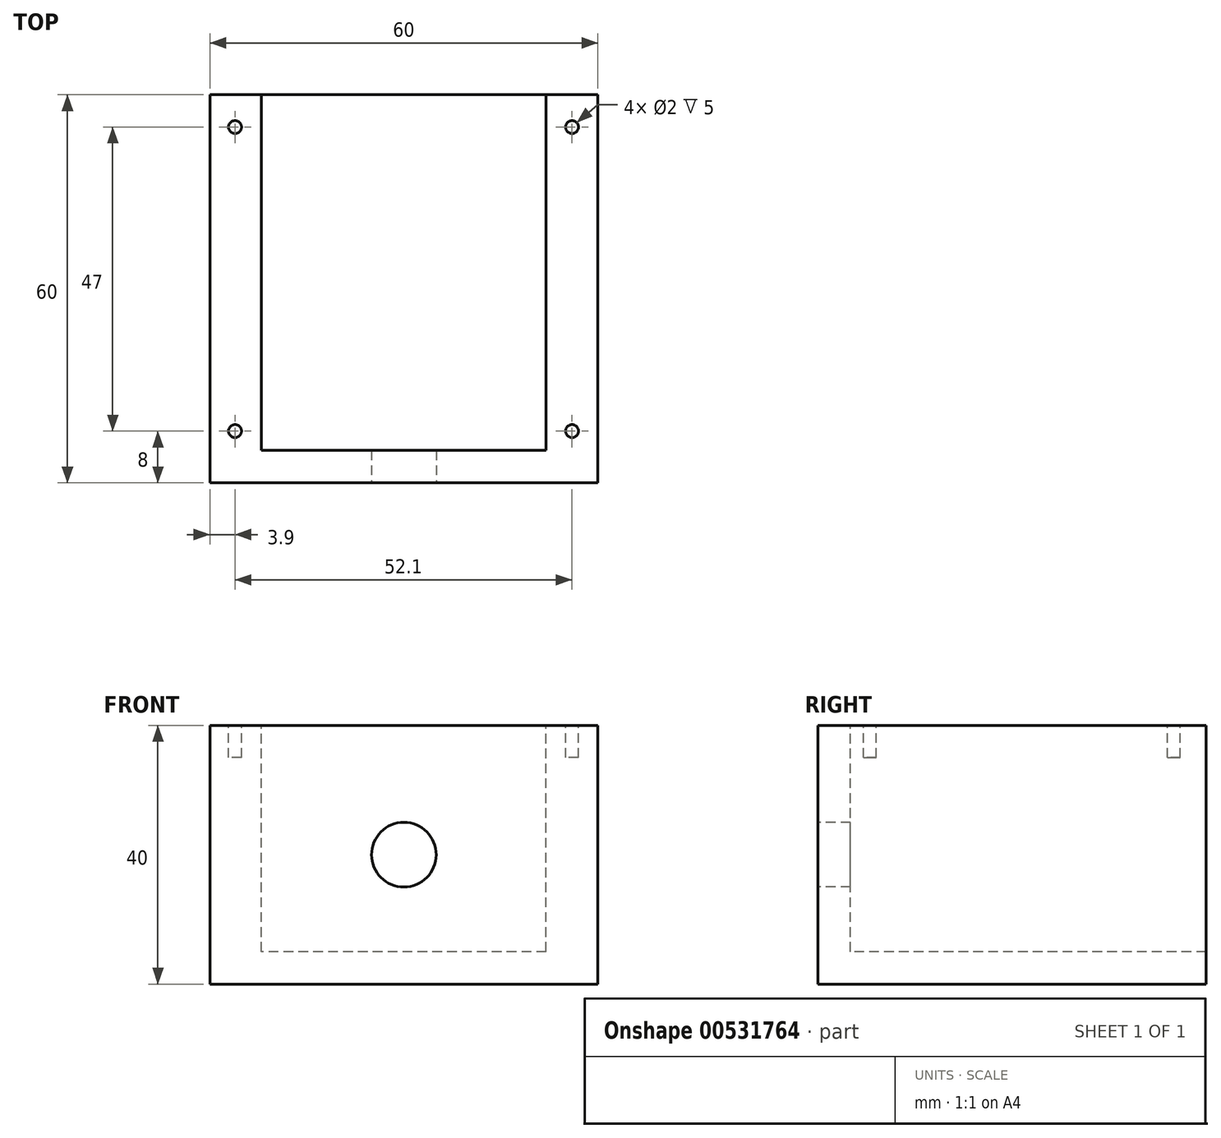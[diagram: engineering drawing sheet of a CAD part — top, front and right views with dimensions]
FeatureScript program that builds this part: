
annotation { "Feature Type Name" : "Feature", "Feature Type Description" : "" }
export const myFeature = defineFeature(function(context is Context, id is Id, definition is map)
    precondition{}
    {
        {
            var Q0;
            Q0=qCreatedBy(makeId("Front.planeOp"),FACE);
            var sketch = newSketch(context, id + "F0", { "sketchPlane" : qUnion([Q0])});
            skLineSegment(sketch, "E0.bottom", {"start": v(30, 20) * mm, "end": v(-30, 20) * mm});
            skLineSegment(sketch, "E0.top", {"start": v(30, -20) * mm, "end": v(-30, -20) * mm});
            skLineSegment(sketch, "E0.left", {"start": v(30, 20) * mm, "end": v(30, -20) * mm});
            skLineSegment(sketch, "E0.right", {"start": v(-30, 20) * mm, "end": v(-30, -20) * mm});
            skPoint(sketch, "E0.middle", {"position": v(0, 0) * mm});
            skSolve(sketch);
        }
        {
            var Q0;
            Q0 = qSketchRegion(id + "F0", true);
            extrude(context, id + "F1", {"entities" : qUnion([Q0]), "depth" : 60 * mm, "offsetDistance" : 25 * mm});
        }
        {
            var Q0;
            Q0=makeQuery(id+"F1.opExtrude","SWEPT_FACE",FACE,{"disambiguationData":[OSD([sQuery(id+"F0.wireOp",EDGE,"E0.bottom")])]});
            var sketch = newSketch(context, id + "F2", { "sketchPlane" : qUnion([Q0])});
            skLineSegment(sketch, "E1.bottom", {"start": v(-22, 0) * mm, "end": v(22, 0) * mm});
            skLineSegment(sketch, "E1.top", {"start": v(-22, -55) * mm, "end": v(22, -55) * mm});
            skLineSegment(sketch, "E1.left", {"start": v(-22, 0) * mm, "end": v(-22, -55) * mm});
            skLineSegment(sketch, "E1.right", {"start": v(22, 0) * mm, "end": v(22, -55) * mm});
            skSolve(sketch);
        }
        {
            var Q0;
            Q0 = qSketchRegion(id + "F2", true);
            extrude(context, id + "F3", {"entities" : qUnion([Q0]), "operationType" : NewBodyOperationType.REMOVE, "oppositeDirection" : true, "depth" : 35 * mm, "offsetDistance" : 25 * mm});
        }
        {
            var Q0;
            Q0=makeQuery(id+"F1.opExtrude","CAP_FACE",FACE,{"disambiguationData":[OSD([sQuery(id+"F0.wireOp",EDGE,"E0.bottom"),sQuery(id+"F0.wireOp",EDGE,"E0.top"),sQuery(id+"F0.wireOp",EDGE,"E0.left"),sQuery(id+"F0.wireOp",EDGE,"E0.right")])],"isStart":false});
            var sketch = newSketch(context, id + "F4", { "sketchPlane" : qUnion([Q0])});
            skCircle(sketch, "E2", {"center": v(0, 0) * mm, "radius": 5 * mm});
            skSolve(sketch);
        }
        {
            var Q0;
            Q0 = qSketchRegion(id + "F4", true);
            extrude(context, id + "F5", {"entities" : qUnion([Q0]), "operationType" : NewBodyOperationType.REMOVE, "oppositeDirection" : true, "depth" : 25 * mm, "offsetDistance" : 25 * mm});
        }
        {
            var Q0;
            Q0=makeQuery(id+"F1.opExtrude","SWEPT_FACE",FACE,{"disambiguationData":[OSD([sQuery(id+"F0.wireOp",EDGE,"E0.bottom")])]});
            var sketch = newSketch(context, id + "F6", { "sketchPlane" : qUnion([Q0])});
            skSolve(sketch);
        }
        {
            var Q0;
            {var subQ0=sQuery(id+"F0.wireOp",EDGE,"E0.bottom");Q0=makeQuery(id+"F6.imprint","IMPRINT",FACE,{"disambiguationData":[TD([[makeQuery(id+"F6.imprint","IMPRINT",EDGE,{"derivedFrom":makeQuery(id+"F1.opExtrude","CAP_EDGE",EDGE,{"disambiguationData":[OSD([subQ0])],"isStart":false})}),-1.0]])]});}
            var sketch = newSketch(context, id + "F7", { "sketchPlane" : qUnion([Q0])});
            skCircle(sketch, "E3", {"center": v(-26.1, -5) * mm, "radius": 1 * mm});
            skCircle(sketch, "E4", {"center": v(26, -5) * mm, "radius": 1 * mm});
            skCircle(sketch, "E5", {"center": v(26, -52) * mm, "radius": 1 * mm});
            skCircle(sketch, "E6", {"center": v(-26.1, -52) * mm, "radius": 1 * mm});
            skLineSegment(sketch, "E7", {"start": v(-25.95, 0) * mm, "end": v(-25.95, -62.78) * mm, "construction": true});
            skLineSegment(sketch, "E8", {"start": v(-25.95, -62.78) * mm, "end": v(25.95, 0) * mm, "construction": true});
            skLineSegment(sketch, "E9", {"start": v(25.95, 0) * mm, "end": v(25.95, -65.5) * mm, "construction": true});
            skSolve(sketch);
        }
        {
            var Q0;
            Q0 = qSketchRegion(id + "F7", true);
            extrude(context, id + "F8", {"entities" : qUnion([Q0]), "operationType" : NewBodyOperationType.REMOVE, "oppositeDirection" : true, "depth" : 5 * mm, "offsetDistance" : 25 * mm});
        }
    });
